# Revit family: ROTHOB_Rothoblaas_Plate_R80
name_source: partatom
category: Structural Connections
units: mm (PartAtom-declared; Revit-internal decimal feet)

## family parameters
Cut with Voids When Loaded = No
Enable cutting in views = Yes
Host = Face
Material for Model Behavior = Steel
OmniClass Number = 23.13.23.11.19.13
Shared = No

## types (1)
- R80100L_185x110x369mm
    AssetType = Fixed
    BIMObjectName = ROTHOB_Rothoblaas_Plate_R80
    Category = Pr_20_76_64_01 - Adjustable post bases
    Color = Grey
    Default Elevation = 1219.2 mm  [stored 4 ft]
    Description = Adjustable post base
    DurationUnit = Years
    Esporta tipo in formato IFC con nome = IfcDiscreteAccessoryType
    ExpectedLife = 50
    Features = Support for timber columns and post bases as bearing elements
    Finish = DAC COAT coating
    GTIN = 8059386079942
    HoleQuantity_nhØ12mm = 8
    HoleQuantity_nvØ5mm = 16
    HoleQuantity_nvØ7.5mm = 8
    ICC-ESCode = DrJ Listing 2406-121
    IfcExportAs = IfcDiscreteAccessoryType
    IfcExportType = USERDEFINED
    Length_L = 110 mm  [stored 0.360892 ft]
    ManufacturerName = ROTHO BLAAS SRL
    ManufacturerURL = www.rothoblaas.com
    Material = S235 Carbon steel with DAC COAT coating
    MinWeight = 3.605 kg
    ModelDisclaimer = The latest version of the data sheets can be found on our website
    ModelNumber = R80100L
    Name = Plate
    NominalLength = 110 mm  [stored 0.360892 ft]
    NominalWidth = 185 mm  [stored 0.606955 ft]
    ObjectMaterial = ROTHOB_Rothoblaas_CarbonSteel_S235_DACCOAT
    OmniClassCode = 23-13 23 11 19 13
    OmniClassTitle = Wood Connectors
    OmniClassVersion = 2012-05-16
    ProductInformation = www.rothoblaas.com/products/fastening/brackets-and-plates/post-bases/r80
    Revision = 000
    Shape = Three-dimensional
    Size = 185x110x369 mm
    Tipo IFC predefinito = USERDEFINED
    UniClass2015Code = Pr_20_76_64_01
    UniClass2015Title = Adjustable post bases
    UniClass2015Version = Products v1.38
    Version = 001
    Width_B = 185 mm  [stored 0.606955 ft]

note: [stored X ft] marks values corroborated as IEEE doubles in the binary element streams (Revit-internal decimal feet)
